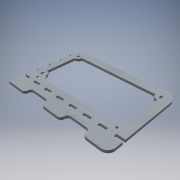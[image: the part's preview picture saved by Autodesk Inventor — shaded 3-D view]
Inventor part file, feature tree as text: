
AUTODESK INVENTOR PART (.ipt)
format: ipt  version: 2018.3 (Build 223284000, 284)  size: 247,808 bytes
history: native  units: mm
features: reference x15, other x5, extrude x3, sketch x3, fillet x2
ambient origin geometry x8: Origin, YZ Plane, XZ Plane, XY Plane, X Axis, Y Axis, Z Axis, Center Point
bodies: Solido1 (feature_tree)
feature tree (28):
  extrude  "Estrusione1"  Depth=165.0mm
  extrude  "Estrusione2"  Depth=33.0mm
  fillet  "Raccordo1"  Radius=10.0mm
  fillet  "Raccordo2"  Radius=33.0mm
  extrude  "Estrusione3"  Depth=10.0mm
  sketch  "Schizzo1"
  reference  "Riferimento4"
  reference  "Riferimento5"
  reference  "Riferimento6"
  reference  "Riferimento8"
  reference  "Riferimento9"
  reference  "Riferimento10"
  reference  "Riferimento11"
  reference  "Riferimento12"
  reference  "Riferimento13"
  reference  "Riferimento14"
  reference  "Riferimento15"
  sketch  "Schizzo2"
  sketch  "Schizzo3"
  reference  "Riferimento16"
  reference  "Riferimento17"
  reference  "Riferimento18"
  reference  "Riferimento19"
  other  "<userpath>\Desktop\Scorbot Hardware\Case Board\caseHw.iam"
  other  "caseHw.iam"
  other  "LC600H-12:1"
  other  "tavolaBase:1"
  other  "Dietro:1"
